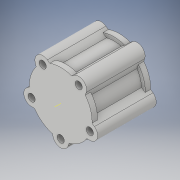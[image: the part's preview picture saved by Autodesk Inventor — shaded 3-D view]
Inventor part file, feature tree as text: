
AUTODESK INVENTOR PART (.ipt)
format: ipt  version: 2018 (Build 220112000, 112)  size: 208,384 bytes
history: native  units: in
note: dims shown in document units (in); Inventor stores cm internally (conversion verified against a paired STEP export)
features: extrude x5, sketch x5, pattern_circular x2, shell x1, other x1, projected_geometry x1
ambient origin geometry x8: Origin, YZ Plane, XZ Plane, XY Plane, X Axis, Y Axis, Z Axis, Center Point
bodies: Solid1 (feature_tree)
feature tree (15):
  extrude  "Extrusion1"  Depth=6.3976in TaperAngle=0.0deg
  shell  "Shell1"  Thickness=0.2362in
  extrude  "Extrusion2"  Depth=6.063in
  extrude  "Extrusion3"  Depth=0.5906in TaperAngle=0.0deg
  extrude  "Extrusion4"  Depth=3.3465in
  other  "Work Axis1"
  pattern_circular  "Circular Pattern1"  Count=5 Angle=360.0deg
  extrude  "Extrusion5"  Depth=6.3976in TaperAngle=360.0deg
  pattern_circular  "Circular Pattern2"  Count=2  [1 undecoded]
  sketch  "Sketch1"  dims[d0=6.063in d1=6.3976in d2=0.0in d3=0.2362in]
  sketch  "Sketch2"  dims[d4=6.8504in d5=6.063in]
  sketch  "Sketch3"  dims[d6=0.5906in d7=0.0in d8=0.5906in d9=0.0in]
  sketch  "Sketch4"  dims[d11=3.3465in d12=0.2474in]
  projected_geometry  "Projected Loop1"
  sketch  "Sketch5"  dims[d13=6.3976in d14=0.0in d15=1.9685in d17=360.0deg d19=1.9685in d20=360.0deg d22=0.7874in d23=6.3976in d24=0.0in d25=1.9685in d26=360.0deg]
note: 1 required parameter value undecoded (feature->parameter linkage not recoverable at this tier; creation-order binding heuristic only, values carry confidence <= 0.55)
